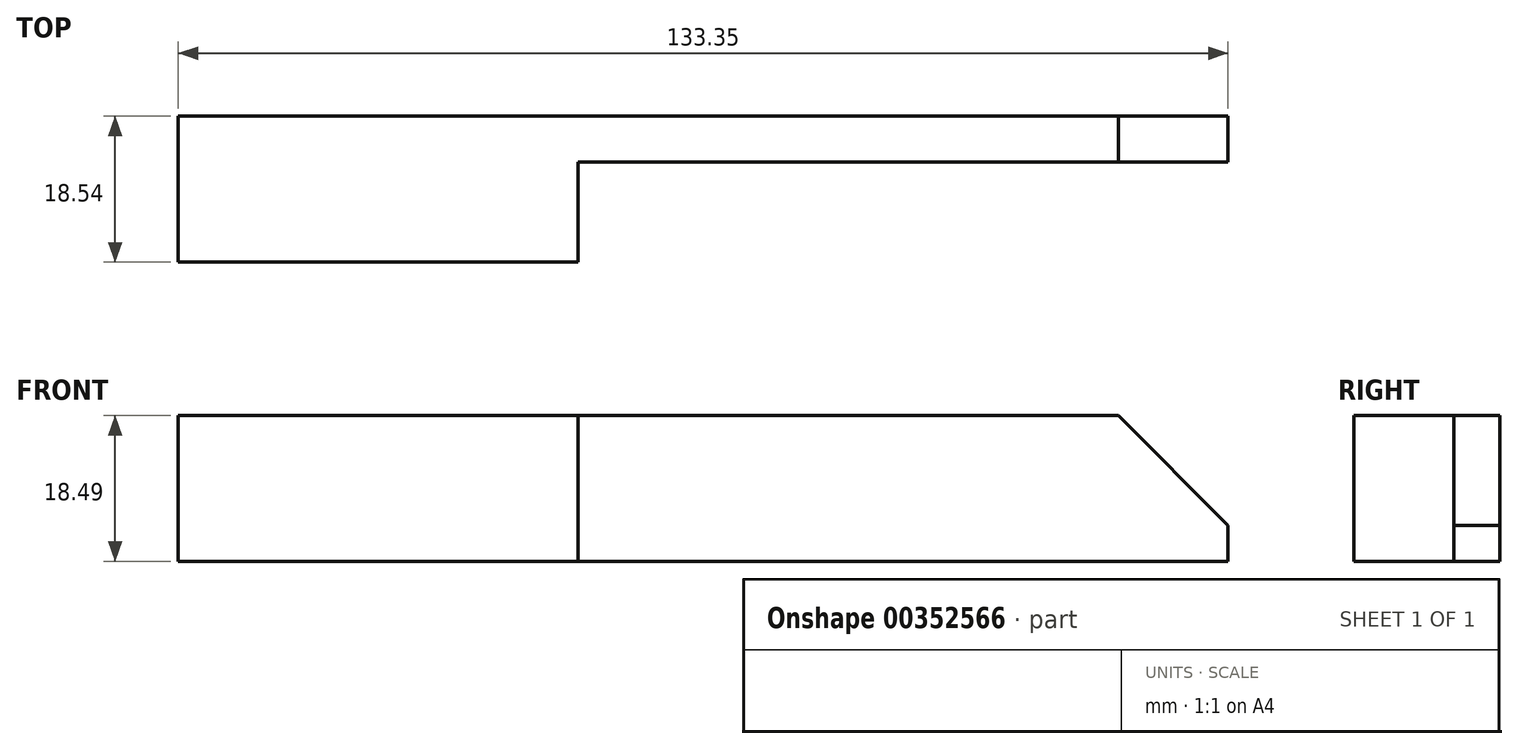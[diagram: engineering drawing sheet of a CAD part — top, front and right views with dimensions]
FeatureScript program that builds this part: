
annotation { "Feature Type Name" : "Feature", "Feature Type Description" : "" }
export const myFeature = defineFeature(function(context is Context, id is Id, definition is map)
    precondition{}
    {
        {
            var Q0;
            Q0=qCreatedBy(makeId("Top.planeOp"),FACE);
            var sketch = newSketch(context, id + "F0", { "sketchPlane" : qUnion([Q0])});
            skLineSegment(sketch, "E0.bottom", {"start": v(0, 0) * mm, "end": v(-133.35, 0) * mm});
            skLineSegment(sketch, "E0.top", {"start": v(0, -5.84) * mm, "end": v(-133.35, -5.84) * mm});
            skLineSegment(sketch, "E0.left", {"start": v(0, 0) * mm, "end": v(0, -5.84) * mm});
            skLineSegment(sketch, "E0.right", {"start": v(-133.35, 0) * mm, "end": v(-133.35, -5.84) * mm});
            skLineSegment(sketch, "E1", {"start": v(-133.35, -18.54) * mm, "end": v(-133.35, -5.84) * mm});
            skLineSegment(sketch, "E2", {"start": v(-133.35, -18.54) * mm, "end": v(-82.55, -18.54) * mm});
            skLineSegment(sketch, "E3", {"start": v(-82.55, -18.54) * mm, "end": v(-82.55, -5.84) * mm});
            skSolve(sketch);
        }
        {
            var Q0;
            Q0 = qSketchRegion(id + "F0", true);
            extrude(context, id + "F1", {"entities" : qUnion([Q0]), "oppositeDirection" : true, "depth" : 18.5 * mm});
        }
        {
            var Q0;
            Q0=makeQuery(id+"F1.opExtrude","SWEPT_FACE",FACE,{"disambiguationData":[OSD([sQuery(id+"F0.wireOp",EDGE,"E0.top")])]});
            var sketch = newSketch(context, id + "F2", { "sketchPlane" : qUnion([Q0])});
            skLineSegment(sketch, "E4.bottom", {"start": v(0, 0) * mm, "end": v(-13.92, 0) * mm});
            skLineSegment(sketch, "E4.top", {"start": v(0, -13.92) * mm, "end": v(-13.92, -13.92) * mm});
            skLineSegment(sketch, "E4.left", {"start": v(0, 0) * mm, "end": v(0, -13.92) * mm});
            skLineSegment(sketch, "E4.right", {"start": v(-13.92, 0) * mm, "end": v(-13.92, -13.92) * mm});
            skLineSegment(sketch, "E5", {"start": v(-13.92, 0) * mm, "end": v(0, -13.92) * mm});
            skSolve(sketch);
        }
        {
            var Q0;
            Q0=makeQuery(id+"F2.imprint","IMPRINT",FACE,{"disambiguationData":[TD([[makeQuery(id+"F2.imprint","IMPRINT",EDGE,{"derivedFrom":sQuery(id+"F2.wireOp",EDGE,"E4.bottom")}),1.0]])]});
            extrude(context, id + "F3", {"entities" : qUnion([Q0]), "operationType" : NewBodyOperationType.REMOVE, "endBound" : BoundingType.THROUGH_ALL, "oppositeDirection" : true, "depth" : 25.4 * mm});
        }
    });
